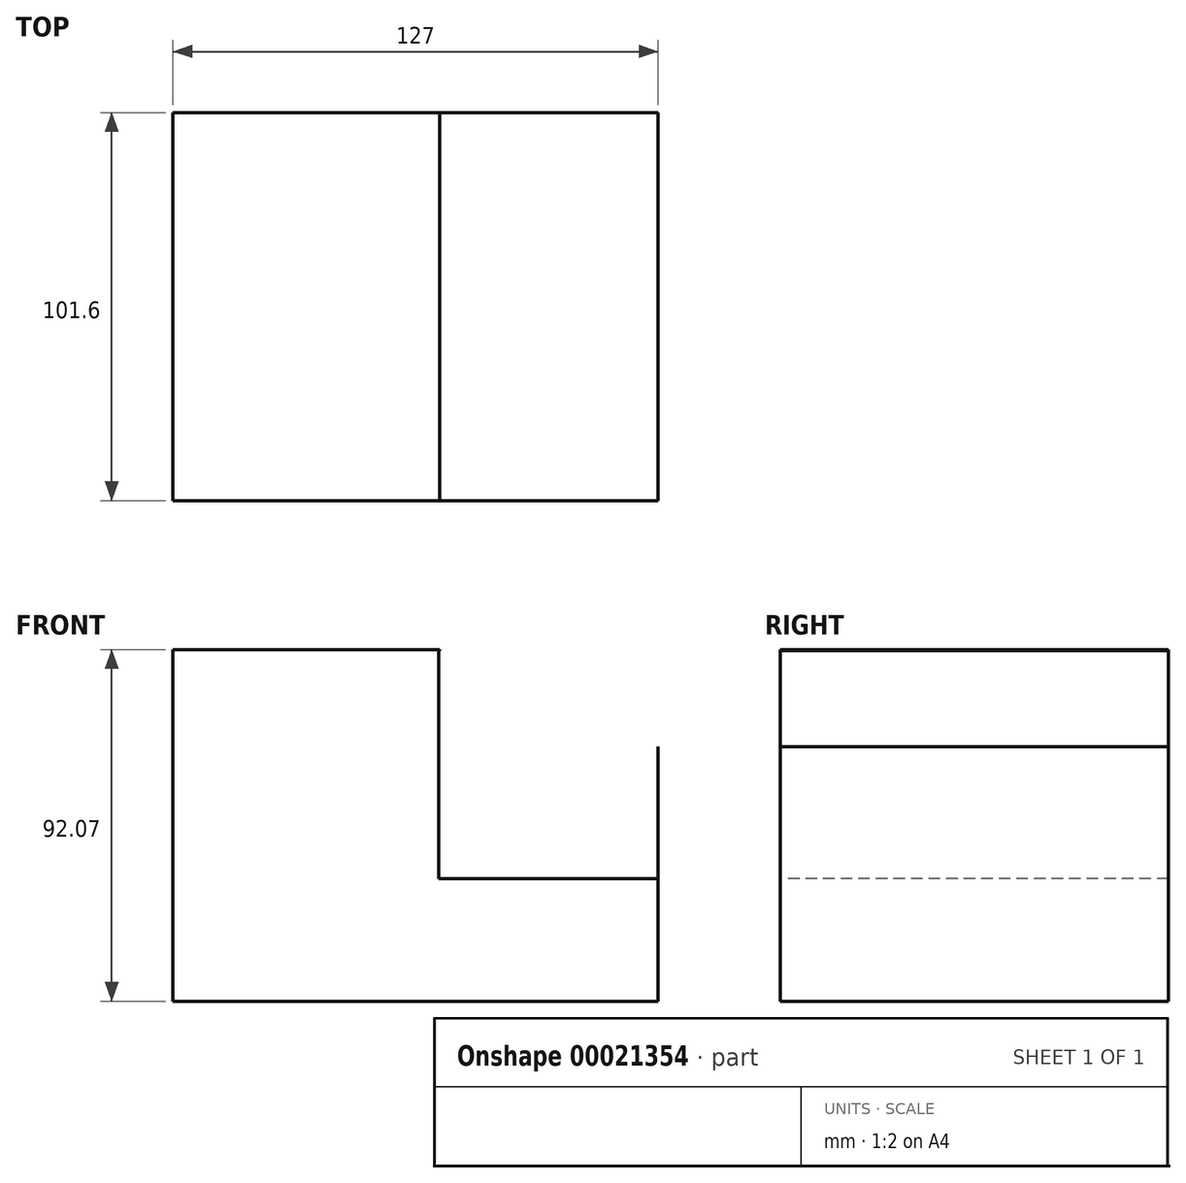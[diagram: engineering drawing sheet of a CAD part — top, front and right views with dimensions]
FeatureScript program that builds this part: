
annotation { "Feature Type Name" : "Feature", "Feature Type Description" : "" }
export const myFeature = defineFeature(function(context is Context, id is Id, definition is map)
    precondition{}
    {
        {
            var Q0;
            Q0=qCreatedBy(makeId("Front.planeOp"),FACE);
            var sketch = newSketch(context, id + "F0", { "sketchPlane" : qUnion([Q0])});
            skLineSegment(sketch, "E0.bottom", {"start": v(-61, 45.75) * mm, "end": v(66, 45.75) * mm});
            skLineSegment(sketch, "E0.top", {"start": v(-61, -46.32) * mm, "end": v(66, -46.32) * mm});
            skLineSegment(sketch, "E0.left", {"start": v(-61, 45.75) * mm, "end": v(-61, -46.32) * mm});
            skLineSegment(sketch, "E0.right", {"start": v(66, 45.75) * mm, "end": v(66, -46.32) * mm});
            skSolve(sketch);
        }
        {
            var Q0;
            Q0=makeQuery(id+"F0.imprint","IMPRINT",FACE,{"disambiguationData":[TD([[makeQuery(id+"F0.imprint","IMPRINT",EDGE,{"derivedFrom":sQuery(id+"F0.wireOp",EDGE,"E0.bottom")}),-1.0]])]});
            extrude(context, id + "F1", {"entities" : qUnion([Q0]), "depth" : 101.6 * mm});
        }
        {
            var Q0;
            Q0=makeQuery(id+"F1.opExtrude","CAP_FACE",FACE,{"disambiguationData":[OSD([sQuery(id+"F0.wireOp",EDGE,"E0.bottom"),sQuery(id+"F0.wireOp",EDGE,"E0.top"),sQuery(id+"F0.wireOp",EDGE,"E0.left"),sQuery(id+"F0.wireOp",EDGE,"E0.right")])],"isStart":false});
            var sketch = newSketch(context, id + "F2", { "sketchPlane" : qUnion([Q0])});
            skLineSegment(sketch, "E1", {"start": v(66, -46.32) * mm, "end": v(66, -14.57) * mm});
            skLineSegment(sketch, "E2", {"start": v(66, -14.57) * mm, "end": v(8.84, -14.57) * mm});
            skSolve(sketch);
        }
        {
            var Q0;
            {var subQ1=sQuery(id+"F2.wireOp",EDGE,"E1");Q0=makeQuery(id+"F2.imprint","IMPRINT",FACE,{"disambiguationData":[TD([[makeQuery(id+"F2.imprint","IMPRINT",EDGE,{"derivedFrom":subQ1}),-1.0]])]});}
            var sketch = newSketch(context, id + "F3", { "sketchPlane" : qUnion([Q0])});
            skLineSegment(sketch, "E3.bottom", {"start": v(8.51, 45.41) * mm, "end": v(65.98, 45.41) * mm});
            skLineSegment(sketch, "E3.top", {"start": v(8.51, -14.22) * mm, "end": v(65.98, -14.22) * mm});
            skLineSegment(sketch, "E3.left", {"start": v(8.51, 45.41) * mm, "end": v(8.51, -14.22) * mm});
            skLineSegment(sketch, "E3.right", {"start": v(65.98, 45.41) * mm, "end": v(65.98, -14.22) * mm});
            skSolve(sketch);
        }
        {
            var Q0;
            Q0 = qSketchRegion(id + "F3", true);
            extrude(context, id + "F4", {"entities" : qUnion([Q0]), "operationType" : NewBodyOperationType.REMOVE, "oppositeDirection" : true, "depth" : 101.6 * mm});
        }
        {
            var Q0;
            Q0=makeQuery(id+"F1.opExtrude","SWEPT_FACE",FACE,{"disambiguationData":[OSD([sQuery(id+"F0.wireOp",EDGE,"E0.bottom")])]});
            var sketch = newSketch(context, id + "F5", { "sketchPlane" : qUnion([Q0])});
            skLineSegment(sketch, "E4", {"start": v(8.82, 0) * mm, "end": v(8.82, -101.6) * mm});
            skLineSegment(sketch, "E5", {"start": v(66, 0) * mm, "end": v(66, -101.6) * mm});
            skLineSegment(sketch, "E6", {"start": v(66, -101.6) * mm, "end": v(8.82, -101.6) * mm});
            skSolve(sketch);
        }
        {
            var Q0;
            Q0 = qSketchRegion(id + "F5", true);
            var Q1;
            {var subQ1=sQuery(id+"F5.wireOp",EDGE,"E4");Q1=makeQuery(id+"F5.imprint","IMPRINT",FACE,{"disambiguationData":[TD([[makeQuery(id+"F5.imprint","IMPRINT",EDGE,{"derivedFrom":subQ1}),1.0]])]});}
            extrude(context, id + "F6", {"entities" : qUnion([Q0, Q1]), "operationType" : NewBodyOperationType.REMOVE, "oppositeDirection" : true, "depth" : 25.4 * mm});
        }
    });
